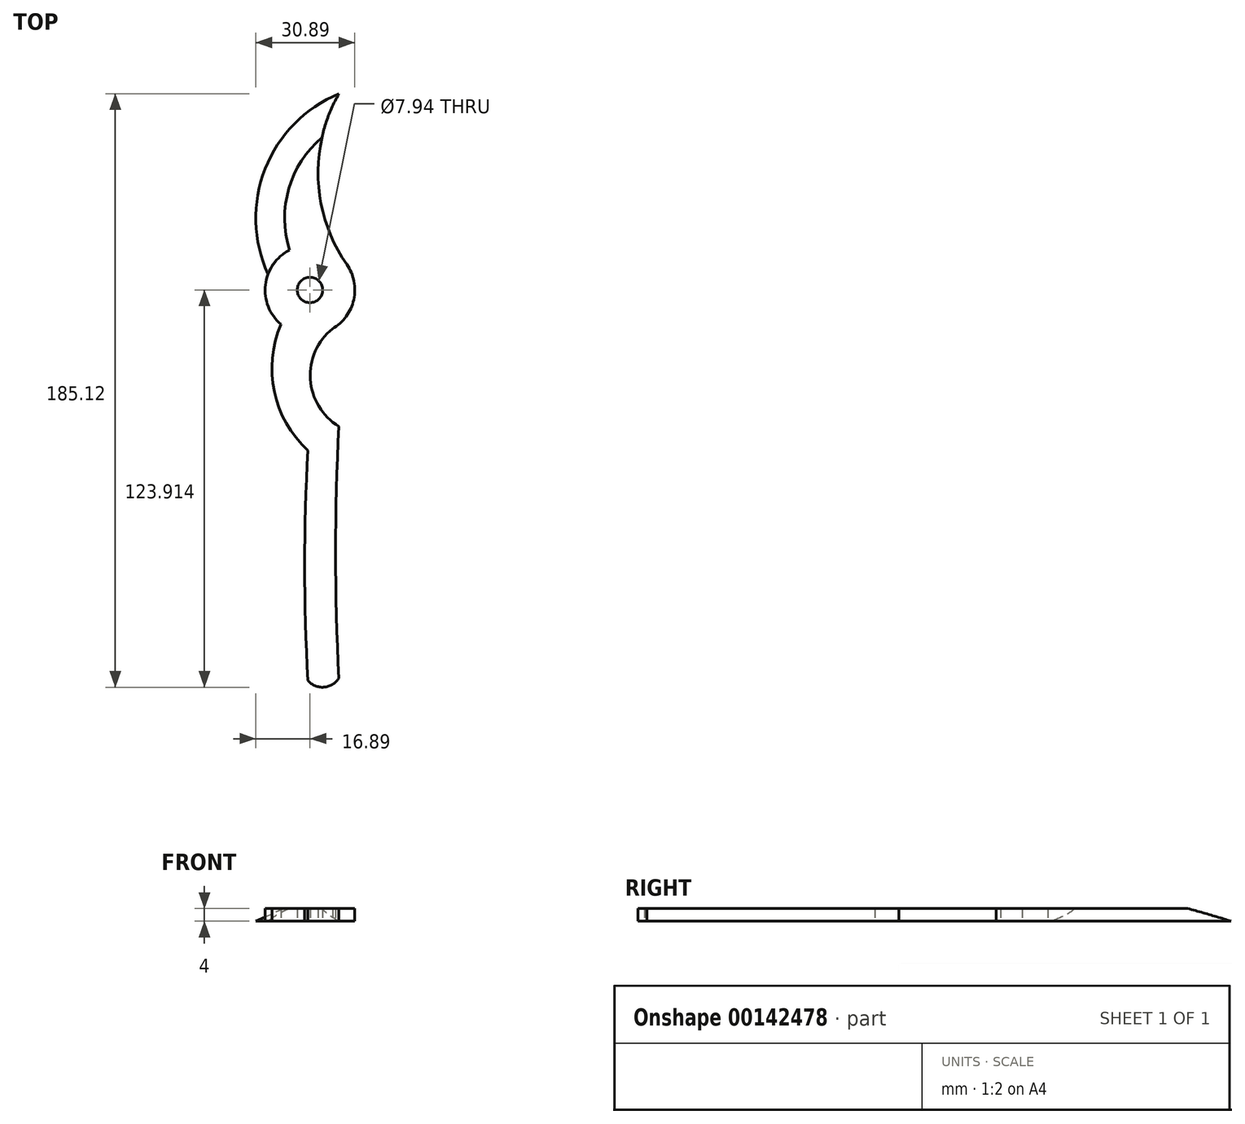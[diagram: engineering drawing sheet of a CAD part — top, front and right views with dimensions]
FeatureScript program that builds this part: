
annotation { "Feature Type Name" : "Feature", "Feature Type Description" : "" }
export const myFeature = defineFeature(function(context is Context, id is Id, definition is map)
    precondition{}
    {
        {
            var Q0;
            Q0=qCreatedBy(makeId("Top.planeOp"),FACE);
            var sketch = newSketch(context, id + "F0", { "sketchPlane" : qUnion([Q0])});
            skLineSegment(sketch, "E0", {"start": v(0, 0) * mm, "end": v(-18, 0) * mm});
            skCircle(sketch, "E1", {"center": v(-9, 10.72) * mm, "radius": 3.97 * mm});
            skCircle(sketch, "E2", {"center": v(-9, 10.72) * mm, "radius": 14 * mm});
            skArc(sketch, "E3.MirrorCS", {"start": v(0, -110.4) * mm, "mid": v(-4.63, -113.18) * mm, "end": v(-9.62, -111.1) * mm});
            skArc(sketch, "E4.MirrorCS", {"start": v(-9.62, -111.1) * mm, "mid": v(-10.63, -75.2) * mm, "end": v(-9.62, -39.3) * mm});
            skArc(sketch, "E5.MirrorCS", {"start": v(0, -110.4) * mm, "mid": v(-1, -71.1) * mm, "end": v(0, -31.8) * mm});
            skArc(sketch, "E6.MirrorCS", {"start": v(-9.62, -39.3) * mm, "mid": v(-20.34, -19.89) * mm, "end": v(-17.03, 2.04) * mm});
            skArc(sketch, "E7.MirrorCS", {"start": v(0, -31.8) * mm, "mid": v(-8.92, -15.9) * mm, "end": v(0, 0) * mm});
            skArc(sketch, "E8", {"start": v(0, 71.93) * mm, "mid": v(-6.43, 44.97) * mm, "end": v(2.49, 18.73) * mm});
            skArc(sketch, "E9", {"start": v(0, 71.93) * mm, "mid": v(-22.99, 48.5) * mm, "end": v(-22.1, 15.68) * mm});
            skArc(sketch, "E10", {"start": v(-4.86, 59.93) * mm, "mid": v(-15.28, 43.16) * mm, "end": v(-14.88, 23.43) * mm});
            skSolve(sketch);
        }
        {
            var Q0;
            Q0 = qSketchRegion(id + "F0", true);
            extrude(context, id + "F1", {"entities" : qUnion([Q0]), "depth" : 4 * mm});
        }
        {
            var Q0;
            Q0=makeQuery(id+"F1.opExtrude","CAP_EDGE",EDGE,{"disambiguationData":[OSD([sQuery(id+"F0.wireOp",EDGE,"E9")])],"isStart":false});
            chamfer(context, id + "F2", {"entities" : qUnion([Q0]), "chamferType" : ChamferType.TWO_OFFSETS, "width1" : 9 * mm, "oppositeDirection" : false, "width2" : 4 * mm, "tangentPropagation" : true});
        }
    });
